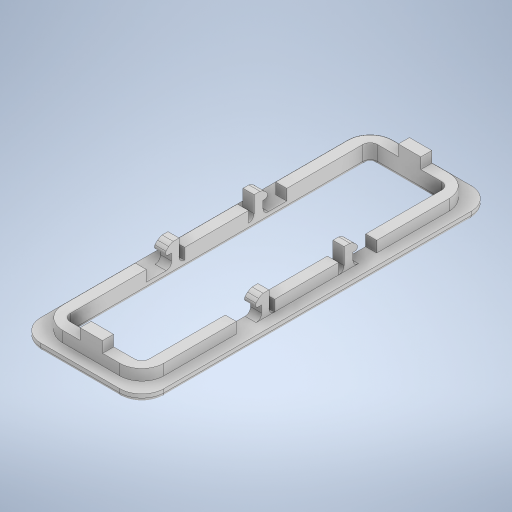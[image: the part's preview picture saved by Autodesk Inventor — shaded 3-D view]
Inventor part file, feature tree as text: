
AUTODESK INVENTOR PART (.ipt)
format: ipt  version: 2023 (Build 270158000, 158)  size: 701,952 bytes
history: native  units: in
note: dims shown in document units (in); Inventor stores cm internally (conversion verified against a paired STEP export)
features: extrude x12, fillet x10, sketch x7, projected_geometry x3, plane x2
ambient origin geometry x8: Origin, YZ Plane, XZ Plane, XY Plane, X Axis, Y Axis, Z Axis, Center Point
bodies: Solid1 (feature_tree), Solid2 (feature_tree)
feature tree (34):
  sketch  "Sketch1"  dims[d0=1.315in d1=3.752in]
  extrude  "Extrusion1"  Depth=3.752in
  extrude  "Extrusion2"  Depth=3.5157in
  plane  "Work Plane1"
  sketch  "Sketch2"  dims[d2=1.0787in d3=3.5157in]
  extrude  "Extrusion3"  Depth=0.1167in
  extrude  "Extrusion4"  Depth=0.1167in
  plane  "Work Plane2"
  extrude  "Extrusion5"  TaperAngle=0.0deg  [1 undecoded]
  fillet  "Fillet1"  Radius=0.0787in
  fillet  "Fillet2"  [1 undecoded]
  sketch  "Sketch4"  dims[d7=0.0in d8=0.1167in]
  extrude  "Extrusion6"  Depth=0.1181in
  extrude  "Extrusion7"  TaperAngle=0.0deg  [1 undecoded]
  extrude  "Extrusion8"  Depth=0.0591in
  sketch  "Sketch5"  dims[d9=0.1167in d10=0.0in d11=0.0787in d12=0.0in d13=-0.1181in]
  extrude  "Extrusion9"  Depth=0.0591in
  extrude  "Extrusion10"  Depth=0.0591in
  extrude  "Extrusion11"  Depth=0.0591in
  extrude  "Extrusion12"  TaperAngle=60.0deg  [1 undecoded]
  fillet  "Fillet4"  Radius=0.1575in
  fillet  "Fillet5"  Radius=0.1181in
  fillet  "Fillet6"  Radius=0.0236in
  fillet  "Fillet7"  Radius=2.1481in
  fillet  "Fillet8"  Radius=0.1575in
  fillet  "Fillet9"  Radius=0.0059in
  fillet  "Fillet10"  Radius=0.1181in
  fillet  "Fillet11"  Radius=0.1181in
  projected_geometry  "Projected Loop1"
  projected_geometry  "Projected Loop2"
  sketch  "Sketch3"  dims[d4=0.0787in d5=0.0in d6=0.1167in]
  projected_geometry  "Projected Loop3"
  sketch  "Sketch6"  dims[d14=0.1181in d15=0.1181in]
  sketch  "Sketch7"  dims[d16=3.2795in d17=0.0in d18=0.1575in d19=0.2362in d20=1.1719in d21=1.1719in d22=60.0deg d23=0.1575in d24=0.1181in d26=0.0236in d27=2.1481in d28=0.0in d29=0.1575in d30=0.0059in d31=0.1181in d32=0.0in d33=0.1181in d34=0.0in d35=0.1181in d36=0.0in d37=0.1181in d38=0.0in d42=0.5087in d43=0.0in d45=0.1167in d46=0.0in d47=0.0787in d48=0.0394in d49=0.0787in d50=0.0394in d51=0.0295in d52=0.0591in d54=0.0591in d55=0.1258in d57=0.1258in d58=0.0059in d59=0.0059in d60=0.1457in d61=0.0394in d62=0.0591in d56=0.0in d63=0.0in]
note: 4 required parameter values undecoded (feature->parameter linkage not recoverable at this tier; creation-order binding heuristic only, values carry confidence <= 0.55)
